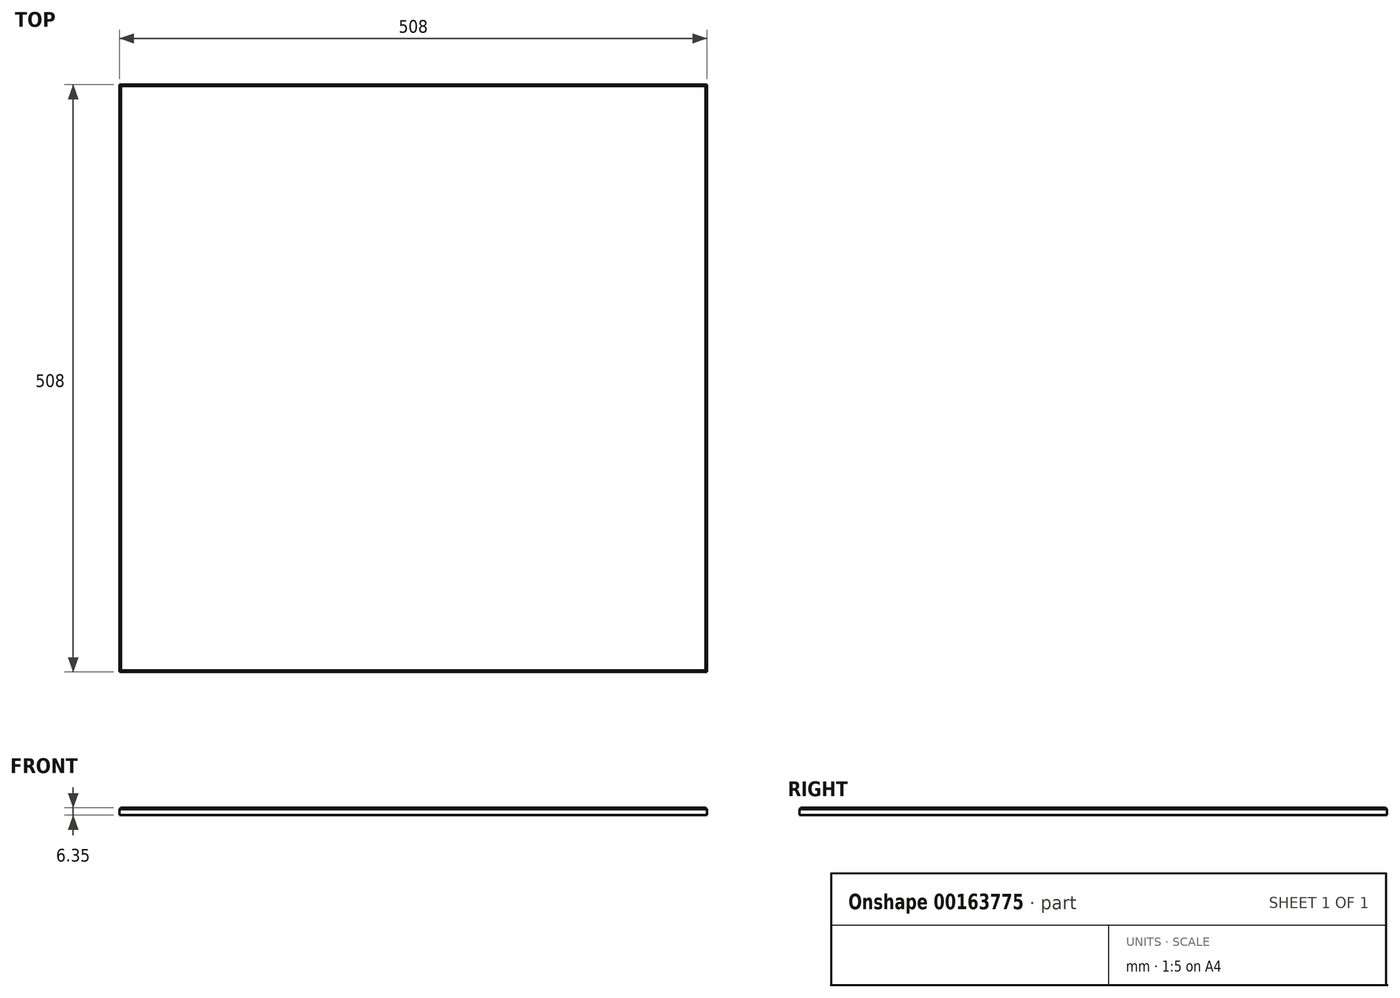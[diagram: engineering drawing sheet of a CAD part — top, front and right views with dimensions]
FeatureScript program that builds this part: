
annotation { "Feature Type Name" : "Feature", "Feature Type Description" : "" }
export const myFeature = defineFeature(function(context is Context, id is Id, definition is map)
    precondition{}
    {
        {
            var Q0;
            Q0=qCreatedBy(makeId("Top.planeOp"),FACE);
            var sketch = newSketch(context, id + "F0", { "sketchPlane" : qUnion([Q0])});
            skLineSegment(sketch, "E0.bottom", {"start": v(254, 254) * mm, "end": v(-254, 254) * mm});
            skLineSegment(sketch, "E0.top", {"start": v(254, -254) * mm, "end": v(-254, -254) * mm});
            skLineSegment(sketch, "E0.left", {"start": v(254, 254) * mm, "end": v(254, -254) * mm});
            skLineSegment(sketch, "E0.right", {"start": v(-254, 254) * mm, "end": v(-254, -254) * mm});
            skPoint(sketch, "E0.middle", {"position": v(0, 0) * mm});
            skSolve(sketch);
        }
        {
            var Q0;
            Q0 = qSketchRegion(id + "F0", true);
            extrude(context, id + "F1", {"entities" : qUnion([Q0]), "depth" : 6.35 * mm});
        }
        {
            var Q0;
            Q0=makeQuery(id+"F1.opExtrude","CAP_FACE",FACE,{"disambiguationData":[OSD([sQuery(id+"F0.wireOp",EDGE,"E0.bottom"),sQuery(id+"F0.wireOp",EDGE,"E0.top"),sQuery(id+"F0.wireOp",EDGE,"E0.left"),sQuery(id+"F0.wireOp",EDGE,"E0.right")])],"isStart":false});
            chamfer(context, id + "F2", {"entities" : qUnion([Q0]), "width" : 1.27 * mm, "tangentPropagation" : true});
        }
    });
